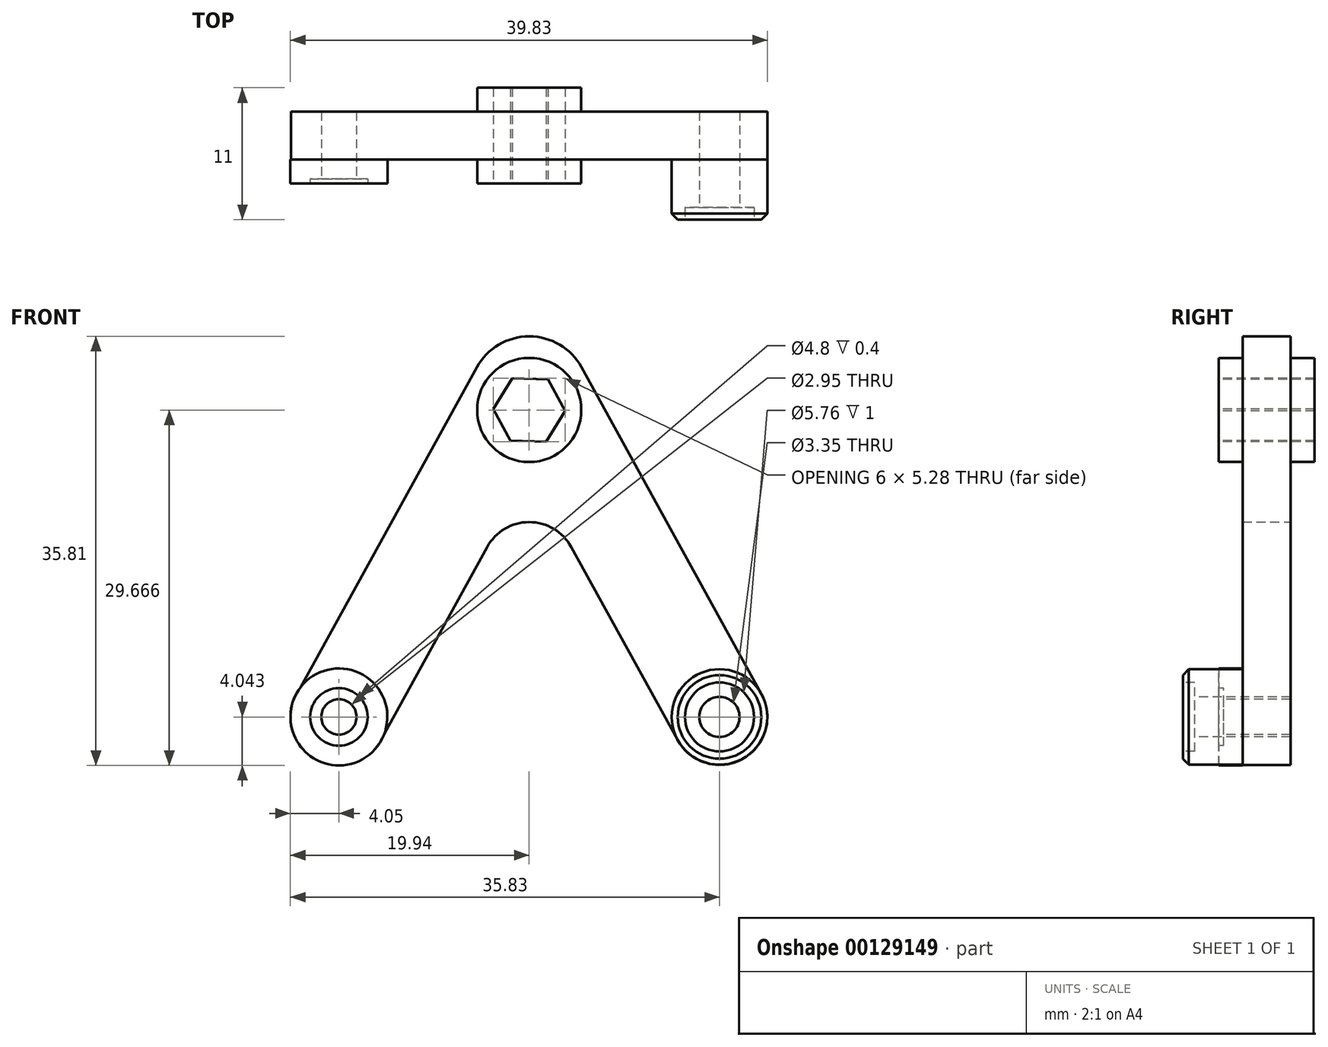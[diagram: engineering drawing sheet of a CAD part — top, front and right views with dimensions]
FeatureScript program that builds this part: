
annotation { "Feature Type Name" : "Feature", "Feature Type Description" : "" }
export const myFeature = defineFeature(function(context is Context, id is Id, definition is map)
    precondition{}
    {
        {
            var Q0;
            Q0=qCreatedBy(makeId("Front.planeOp"),FACE);
            var sketch = newSketch(context, id + "F0", { "sketchPlane" : qUnion([Q0])});
            skArc(sketch, "E0", {"start": v(4.38, 25) * mm, "mid": v(0, 27.6) * mm, "end": v(-4.38, 25) * mm});
            skArc(sketch, "E1", {"start": v(3.5, 10.02) * mm, "mid": v(0, 12.09) * mm, "end": v(-3.5, 10.02) * mm});
            skArc(sketch, "E2", {"start": v(-19.4, -2.25) * mm, "mid": v(-17.82, -7.68) * mm, "end": v(-12.39, -6.1) * mm});
            skArc(sketch, "E3.MirrorC", {"start": v(19.4, -2.25) * mm, "mid": v(17.82, -7.68) * mm, "end": v(12.39, -6.1) * mm});
            skLineSegment(sketch, "E4", {"start": v(-19.4, -2.25) * mm, "end": v(-4.38, 25) * mm});
            skLineSegment(sketch, "E5", {"start": v(3.5, 10.02) * mm, "end": v(12.39, -6.1) * mm});
            skLineSegment(sketch, "E6", {"start": v(19.4, -2.25) * mm, "end": v(4.38, 25) * mm});
            skLineSegment(sketch, "E7", {"start": v(-12.39, -6.1) * mm, "end": v(-3.5, 10.02) * mm});
            skSolve(sketch);
        }
        {
            var Q0;
            Q0 = qSketchRegion(id + "F0", true);
            extrude(context, id + "F1", {"entities" : qUnion([Q0]), "depth" : 4 * mm});
        }
        {
            var Q0;
            Q0=makeQuery(id+"F1.opExtrude","CAP_FACE",FACE,{"disambiguationData":[OSD([sQuery(id+"F0.wireOp",EDGE,"E0"),sQuery(id+"F0.wireOp",EDGE,"E1"),sQuery(id+"F0.wireOp",EDGE,"E2"),sQuery(id+"F0.wireOp",EDGE,"E3.MirrorC"),sQuery(id+"F0.wireOp",EDGE,"E4"),sQuery(id+"F0.wireOp",EDGE,"E5"),sQuery(id+"F0.wireOp",EDGE,"E6"),sQuery(id+"F0.wireOp",EDGE,"E7")])],"isStart":false});
            var sketch = newSketch(context, id + "F2", { "sketchPlane" : qUnion([Q0])});
            skCircle(sketch, "E8", {"center": v(0, 21.45) * mm, "radius": 4.35 * mm});
            skSolve(sketch);
        }
        {
            var Q0;
            Q0 = qSketchRegion(id + "F2", true);
            extrude(context, id + "F3", {"entities" : qUnion([Q0]), "operationType" : NewBodyOperationType.ADD, "depth" : 2 * mm, "hasSecondDirection" : true, "secondDirectionOppositeDirection" : true, "secondDirectionDepth" : 6 * mm});
        }
        {
            var Q0;
            Q0=makeQuery(id+"F3.opExtrude","CAP_FACE",FACE,{"disambiguationData":[OSD([sQuery(id+"F2.wireOp",EDGE,"E8")])],"isStart":false});
            var sketch = newSketch(context, id + "F4", { "sketchPlane" : qUnion([Q0])});
            skCircle(sketch, "E9.cCircle", {"center": v(0, 21.45) * mm, "radius": 3 * mm, "construction": true});
            skLineSegment(sketch, "E9.0", {"start": v(1.43, 18.8) * mm, "end": v(-1.57, 18.9) * mm});
            skLineSegment(sketch, "E9.1", {"start": v(-1.57, 18.9) * mm, "end": v(-3, 21.53) * mm});
            skLineSegment(sketch, "E9.2", {"start": v(-3, 21.53) * mm, "end": v(-1.43, 24.08) * mm});
            skLineSegment(sketch, "E9.3", {"start": v(-1.43, 24.08) * mm, "end": v(1.57, 24) * mm});
            skLineSegment(sketch, "E9.4", {"start": v(1.57, 24) * mm, "end": v(3, 21.36) * mm});
            skLineSegment(sketch, "E9.5", {"start": v(3, 21.36) * mm, "end": v(1.43, 18.8) * mm});
            skSolve(sketch);
        }
        {
            var Q0;
            Q0=makeQuery(id+"F4.imprint","IMPRINT",FACE,{"disambiguationData":[TD([[makeQuery(id+"F4.imprint","IMPRINT",EDGE,{"derivedFrom":sQuery(id+"F4.wireOp",EDGE,"E9.0")}),-1.0]])]});
            extrude(context, id + "F5", {"entities" : qUnion([Q0]), "operationType" : NewBodyOperationType.REMOVE, "oppositeDirection" : true, "depth" : 25 * mm});
        }
        {
            var Q0;
            Q0=makeQuery(id+"F1.opExtrude","CAP_FACE",FACE,{"disambiguationData":[OSD([sQuery(id+"F0.wireOp",EDGE,"E0"),sQuery(id+"F0.wireOp",EDGE,"E1"),sQuery(id+"F0.wireOp",EDGE,"E2"),sQuery(id+"F0.wireOp",EDGE,"E3.MirrorC"),sQuery(id+"F0.wireOp",EDGE,"E4"),sQuery(id+"F0.wireOp",EDGE,"E5"),sQuery(id+"F0.wireOp",EDGE,"E6"),sQuery(id+"F0.wireOp",EDGE,"E7")])],"isStart":false});
            var sketch = newSketch(context, id + "F6", { "sketchPlane" : qUnion([Q0])});
            skCircle(sketch, "E10", {"center": v(-15.89, -4.18) * mm, "radius": 4.05 * mm});
            skSolve(sketch);
        }
        {
            var Q0;
            Q0 = qSketchRegion(id + "F6", true);
            extrude(context, id + "F7", {"entities" : qUnion([Q0]), "operationType" : NewBodyOperationType.ADD, "depth" : 2 * mm});
        }
        {
            var Q0;
            Q0=makeQuery(id+"F7.opExtrude","CAP_FACE",FACE,{"disambiguationData":[OSD([sQuery(id+"F6.wireOp",EDGE,"E10")])],"isStart":false});
            var sketch = newSketch(context, id + "F8", { "sketchPlane" : qUnion([Q0])});
            skCircle(sketch, "E11", {"center": v(-15.89, -4.18) * mm, "radius": 2.4 * mm});
            skSolve(sketch);
        }
        {
            var Q0;
            Q0 = qSketchRegion(id + "F8", true);
            extrude(context, id + "F9", {"entities" : qUnion([Q0]), "operationType" : NewBodyOperationType.REMOVE, "oppositeDirection" : true, "depth" : .4 * mm});
        }
        {
            var Q0;
            Q0=makeQuery(id+"F9.boolean.opBoolean","COPY",FACE,{"derivedFrom":makeQuery(id+"F9.opExtrude","CAP_FACE",FACE,{"disambiguationData":[OSD([sQuery(id+"F8.wireOp",EDGE,"E11")])],"isStart":false})});
            var sketch = newSketch(context, id + "F10", { "sketchPlane" : qUnion([Q0])});
            skCircle(sketch, "E12", {"center": v(-15.89, -4.18) * mm, "radius": 1.47 * mm});
            skSolve(sketch);
        }
        {
            var Q0;
            Q0 = qSketchRegion(id + "F10", true);
            extrude(context, id + "F11", {"entities" : qUnion([Q0]), "operationType" : NewBodyOperationType.REMOVE, "oppositeDirection" : true, "depth" : 25 * mm});
        }
        {
            var Q0;
            Q0=makeQuery(id+"F1.opExtrude","CAP_FACE",FACE,{"disambiguationData":[OSD([sQuery(id+"F0.wireOp",EDGE,"E0"),sQuery(id+"F0.wireOp",EDGE,"E1"),sQuery(id+"F0.wireOp",EDGE,"E2"),sQuery(id+"F0.wireOp",EDGE,"E3.MirrorC"),sQuery(id+"F0.wireOp",EDGE,"E4"),sQuery(id+"F0.wireOp",EDGE,"E5"),sQuery(id+"F0.wireOp",EDGE,"E6"),sQuery(id+"F0.wireOp",EDGE,"E7")])],"isStart":false});
            var sketch = newSketch(context, id + "F12", { "sketchPlane" : qUnion([Q0])});
            skCircle(sketch, "E13", {"center": v(15.89, -4.18) * mm, "radius": 3.99 * mm});
            skSolve(sketch);
        }
        {
            var Q0;
            Q0 = qSketchRegion(id + "F12", true);
            extrude(context, id + "F13", {"entities" : qUnion([Q0]), "operationType" : NewBodyOperationType.ADD, "depth" : 5 * mm});
        }
        {
            var Q0;
            Q0=makeQuery(id+"F13.opExtrude","CAP_FACE",FACE,{"disambiguationData":[OSD([sQuery(id+"F12.wireOp",EDGE,"E13")])],"isStart":false});
            var sketch = newSketch(context, id + "F14", { "sketchPlane" : qUnion([Q0])});
            skCircle(sketch, "E14", {"center": v(15.89, -4.18) * mm, "radius": 2.88 * mm});
            skSolve(sketch);
        }
        {
            var Q0;
            Q0 = qSketchRegion(id + "F14", true);
            extrude(context, id + "F15", {"entities" : qUnion([Q0]), "operationType" : NewBodyOperationType.REMOVE, "oppositeDirection" : true, "depth" : 1 * mm});
        }
        {
            var Q0;
            Q0=makeQuery(id+"F15.boolean.opBoolean","COPY",FACE,{"derivedFrom":makeQuery(id+"F15.opExtrude","CAP_FACE",FACE,{"disambiguationData":[OSD([sQuery(id+"F14.wireOp",EDGE,"E14")])],"isStart":false})});
            var sketch = newSketch(context, id + "F16", { "sketchPlane" : qUnion([Q0])});
            skCircle(sketch, "E15", {"center": v(15.89, -4.18) * mm, "radius": 1.68 * mm});
            skSolve(sketch);
        }
        {
            var Q0;
            Q0 = qSketchRegion(id + "F16", true);
            extrude(context, id + "F17", {"entities" : qUnion([Q0]), "operationType" : NewBodyOperationType.REMOVE, "oppositeDirection" : true, "depth" : 25 * mm});
        }
        {
            var Q0;
            Q0=makeQuery(id+"F13.opExtrude","CAP_EDGE",EDGE,{"disambiguationData":[OSD([sQuery(id+"F12.wireOp",EDGE,"E13")])],"isStart":false});
            chamfer(context, id + "F18", {"entities" : qUnion([Q0]), "width" : .5 * mm, "tangentPropagation" : true});
        }
    });
